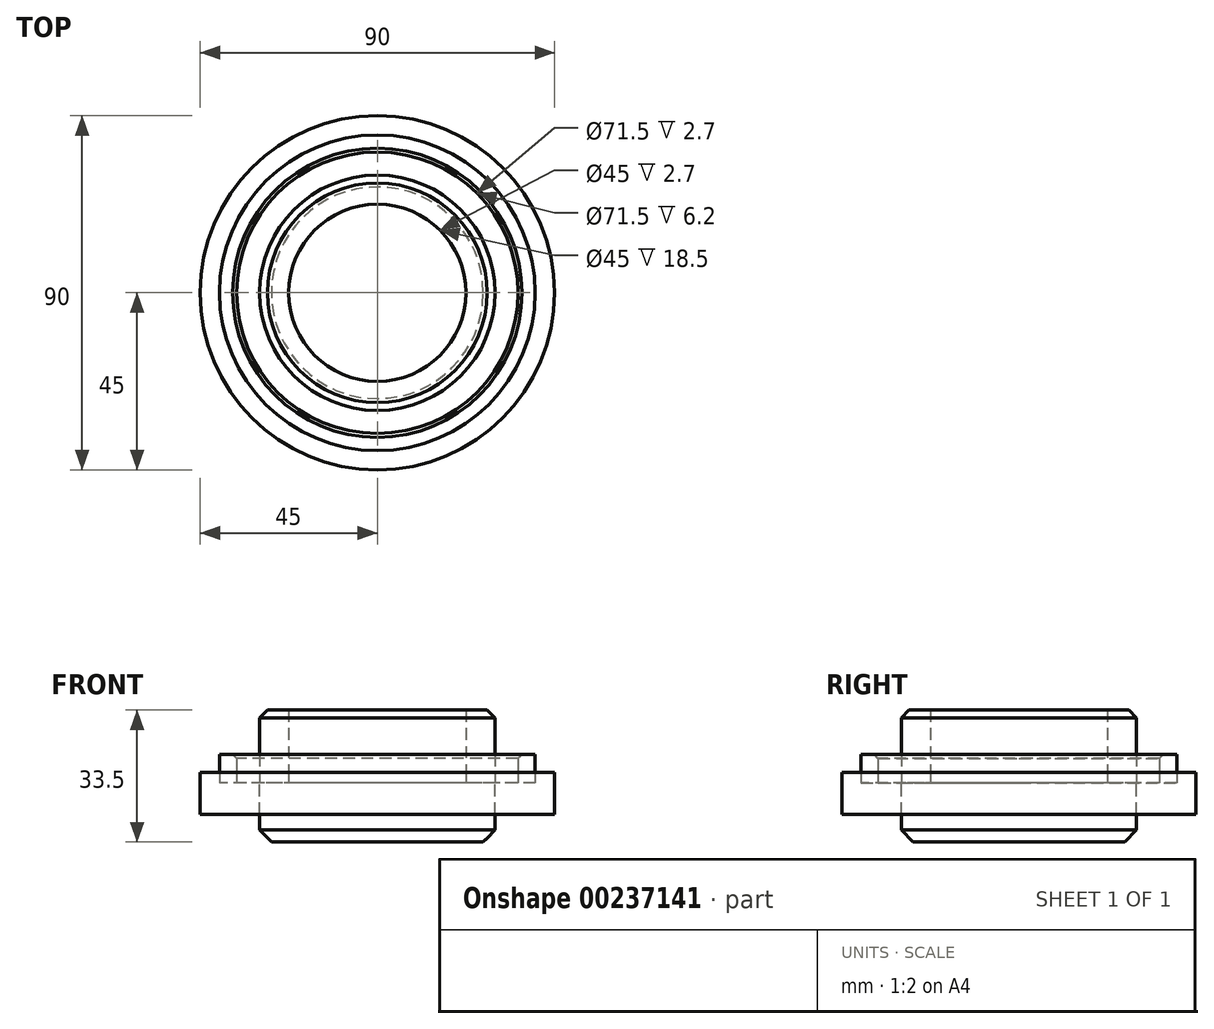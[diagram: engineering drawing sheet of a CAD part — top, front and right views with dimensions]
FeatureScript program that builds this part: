
annotation { "Feature Type Name" : "Feature", "Feature Type Description" : "" }
export const myFeature = defineFeature(function(context is Context, id is Id, definition is map)
    precondition{}
    {
        {
            var Q0;
            Q0=qCreatedBy(makeId("Top.planeOp"),FACE);
            var sketch = newSketch(context, id + "F0", { "sketchPlane" : qUnion([Q0])});
            skCircle(sketch, "E0", {"center": v(0, 0) * mm, "radius": 40.1 * mm});
            skCircle(sketch, "E1", {"center": v(0, 0) * mm, "radius": 29.9 * mm});
            skCircle(sketch, "E2", {"center": v(0, 0) * mm, "radius": 35.75 * mm});
            skSolve(sketch);
        }
        {
            var Q0;
            Q0=qCreatedBy(makeId("Top.planeOp"),FACE);
            var sketch = newSketch(context, id + "F1", { "sketchPlane" : qUnion([Q0])});
            skCircle(sketch, "E3", {"center": v(0, 0) * mm, "radius": 45 * mm});
            skSolve(sketch);
        }
        {
            var Q0;
            Q0=qCreatedBy(makeId("Top.planeOp"),FACE);
            var sketch = newSketch(context, id + "F2", { "sketchPlane" : qUnion([Q0])});
            skCircle(sketch, "E4", {"center": v(0, 0) * mm, "radius": 22.5 * mm});
            skSolve(sketch);
        }
        {
            var Q0;
            Q0=makeQuery(id+"F0.imprint","IMPRINT",FACE,{"disambiguationData":[TD([[makeQuery(id+"F0.imprint","IMPRINT",EDGE,{"derivedFrom":sQuery(id+"F0.wireOp",EDGE,"E1")}),1.0]])]});
            var Q1;
            Q1=makeQuery(id+"F0.imprint","IMPRINT",FACE,{"disambiguationData":[TD([[makeQuery(id+"F0.imprint","IMPRINT",EDGE,{"derivedFrom":sQuery(id+"F0.wireOp",EDGE,"E0")}),1.0]])]});
            extrude(context, id + "F3", {"entities" : qUnion([Q0, Q1]), "flatOperationType" : FlatOperationType.REMOVE, "offsetDistance" : 25 * mm, "depth" : 7.2 * mm, "domain" : OperationDomain.MODEL});
        }
        {
            var Q0;
            Q0=qSketchRegion(id+"F1",true);
            extrude(context, id + "F4", {"entities" : qUnion([Q0]), "oppositeDirection" : true, "depth" : 8 * mm, "hasSecondDirection" : true, "secondDirectionOppositeDirection" : false, "secondDirectionDepth" : 2.7 * mm});
        }
        {
            var Q0;
            Q0=makeQuery(id+"F0.imprint","IMPRINT",FACE,{"disambiguationData":[TD([[makeQuery(id+"F0.imprint","IMPRINT",EDGE,{"derivedFrom":sQuery(id+"F0.wireOp",EDGE,"E1")}),-1.0]])]});
            var Q1;
            Q1=sQuery(id+"F0.wireOp",EDGE,"E0");
            var Q2;
            Q2=sQuery(id+"F0.wireOp",EDGE,"E2");
            extrude(context, id + "F5", {"entities" : qUnion([Q0]), "operationType" : NewBodyOperationType.REMOVE, "surfaceEntities" : qUnion([Q1, Q2]), "depth" : 6.7 * mm});
        }
        {
            var Q0;
            Q0=makeQuery(id+"F3.opExtrude","CAP_EDGE",EDGE,{"disambiguationData":[OSD([sQuery(id+"F0.wireOp",EDGE,"E2")])],"isStart":false});
            chamfer(context, id + "F6", {"entities" : qUnion([Q0]), "width" : 1 * mm, "tangentPropagation" : true});
        }
        {
            var Q0;
            Q0=makeQuery(id+"F3.opExtrude","CAP_FACE",FACE,{"disambiguationData":[OSD([sQuery(id+"F0.wireOp",EDGE,"E1")])],"isStart":false});
            extrude(context, id + "F7", {"entities" : qUnion([Q0]), "operationType" : NewBodyOperationType.ADD, "depth" : 11.3 * mm});
        }
        {
            var Q0;
            Q0=makeQuery(id+"F4.opExtrude","CAP_FACE",FACE,{"disambiguationData":[OSD([sQuery(id+"F1.wireOp",EDGE,"E3")])],"isStart":false});
            var sketch = newSketch(context, id + "F8", { "sketchPlane" : qUnion([Q0])});
            skArc(sketch, "E5", {"start": v(-33.76, 0) * mm, "mid": v(0, 33.76) * mm, "end": v(33.76, 0) * mm});
            skSolve(sketch);
        }
        {
            var Q0;
            Q0=makeQuery(id+"F7.opExtrude","CAP_EDGE",EDGE,{"disambiguationData":[OSD([sQuery(id+"F0.wireOp",EDGE,"E1")])],"isStart":false});
            chamfer(context, id + "F9", {"entities" : qUnion([Q0]), "width" : 2 * mm, "tangentPropagation" : true});
        }
        {
            var Q0;
            Q0=makeQuery(id+"F2.imprint","IMPRINT",FACE,{"disambiguationData":[TD([[makeQuery(id+"F2.imprint","IMPRINT",EDGE,{"derivedFrom":sQuery(id+"F2.wireOp",EDGE,"E4")}),1.0]])]});
            var Q1;
            Q1=sQuery(id+"F2.wireOp",EDGE,"E4");
            extrude(context, id + "F10", {"entities" : qUnion([Q0]), "operationType" : NewBodyOperationType.REMOVE, "surfaceEntities" : qUnion([Q1]), "depth" : 40 * mm});
        }
        {
            var Q0;
            Q0=makeQuery(id+"F0.imprint","IMPRINT",FACE,{"disambiguationData":[TD([[makeQuery(id+"F0.imprint","IMPRINT",EDGE,{"derivedFrom":sQuery(id+"F0.wireOp",EDGE,"E1")}),1.0]])]});
            var Q1;
            Q1=sQuery(id+"F0.wireOp",EDGE,"E1");
            extrude(context, id + "F11", {"entities" : qUnion([Q0]), "surfaceEntities" : qUnion([Q1]), "depth" : -15 * mm});
        }
        {
            var Q0;
            Q0=makeQuery(id+"F11.opExtrude","CAP_EDGE",EDGE,{"disambiguationData":[OSD([sQuery(id+"F0.wireOp",EDGE,"E1")])],"isStart":false});
            chamfer(context, id + "F12", {"entities" : qUnion([Q0]), "width" : 3 * mm, "tangentPropagation" : true});
        }
    });
